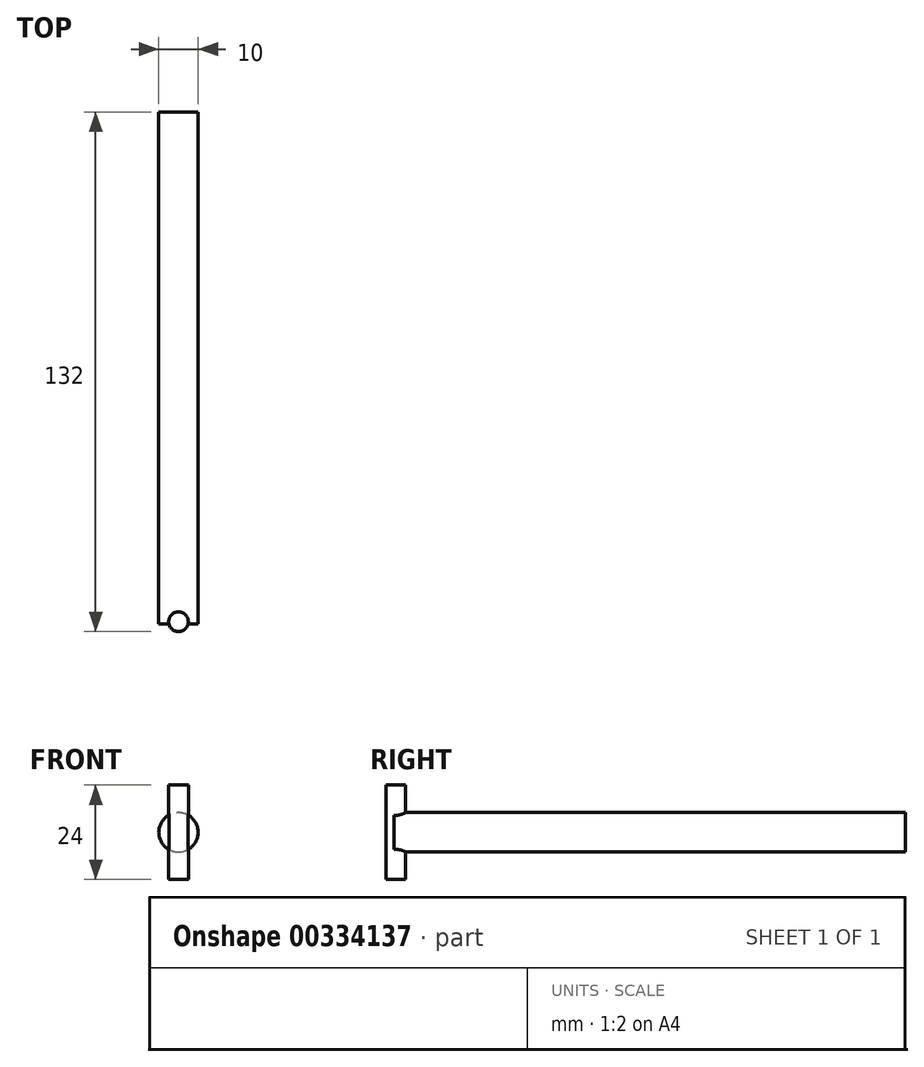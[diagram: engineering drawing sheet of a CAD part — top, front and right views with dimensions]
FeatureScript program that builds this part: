
annotation { "Feature Type Name" : "Feature", "Feature Type Description" : "" }
export const myFeature = defineFeature(function(context is Context, id is Id, definition is map)
    precondition{}
    {
        {
            var Q0;
            Q0=qCreatedBy(makeId("Front.planeOp"),FACE);
            var sketch = newSketch(context, id + "F0", { "sketchPlane" : qUnion([Q0])});
            skCircle(sketch, "E0", {"center": v(0, 0) * mm, "radius": 5 * mm});
            skSolve(sketch);
        }
        {
            var Q0;
            Q0=qSketchRegion(id+"F0",true);
            extrude(context, id + "F1", {"entities" : qUnion([Q0]), "depth" : 130 * mm});
        }
        {
            var Q0;
            Q0=qCreatedBy(makeId("Top.planeOp"),FACE);
            var sketch = newSketch(context, id + "F2", { "sketchPlane" : qUnion([Q0])});
            skCircle(sketch, "E1", {"center": v(0, -129.5) * mm, "radius": 2.5 * mm});
            skSolve(sketch);
        }
        {
            var Q0;
            Q0=qSketchRegion(id+"F2",true);
            extrude(context, id + "F3", {"entities" : qUnion([Q0]), "operationType" : NewBodyOperationType.ADD, "depth" : 24 * mm, "symmetric" : true});
        }
    });
